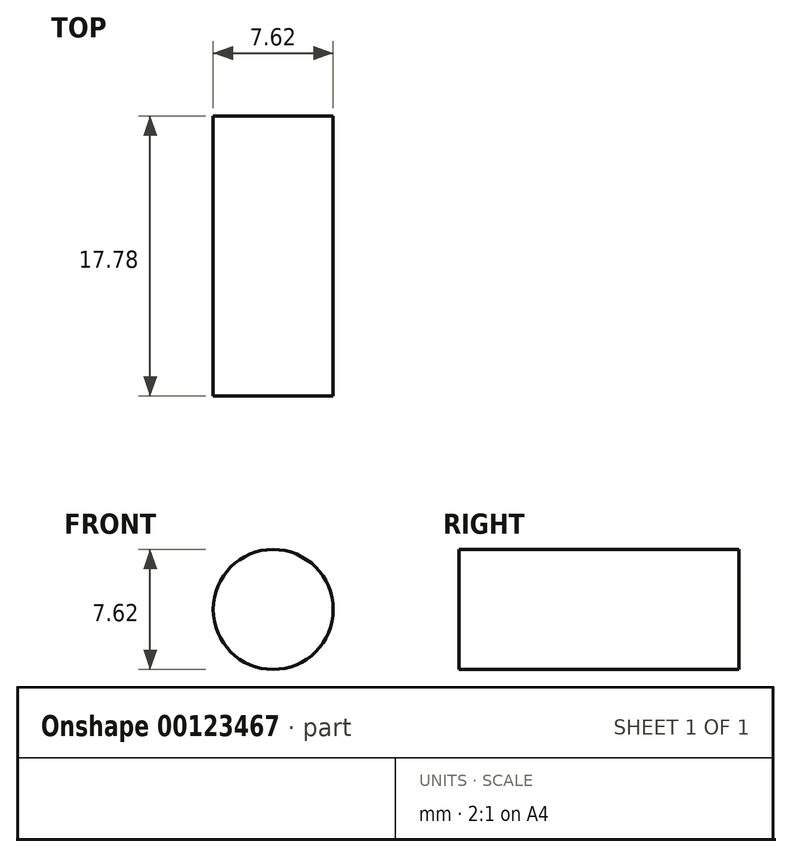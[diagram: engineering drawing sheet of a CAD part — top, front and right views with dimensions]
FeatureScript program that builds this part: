
annotation { "Feature Type Name" : "Feature", "Feature Type Description" : "" }
export const myFeature = defineFeature(function(context is Context, id is Id, definition is map)
    precondition{}
    {
        {
            var Q0;
            Q0=qCreatedBy(makeId("Front.planeOp"),FACE);
            var sketch = newSketch(context, id + "F0", { "sketchPlane" : qUnion([Q0])});
            skCircle(sketch, "E0", {"center": v(0, 0) * mm, "radius": 3.81 * mm});
            skSolve(sketch);
        }
        {
            var Q0;
            Q0 = qSketchRegion(id + "F0", true);
            extrude(context, id + "F1", {"entities" : qUnion([Q0]), "depth" : 17.78 * mm});
        }
    });
